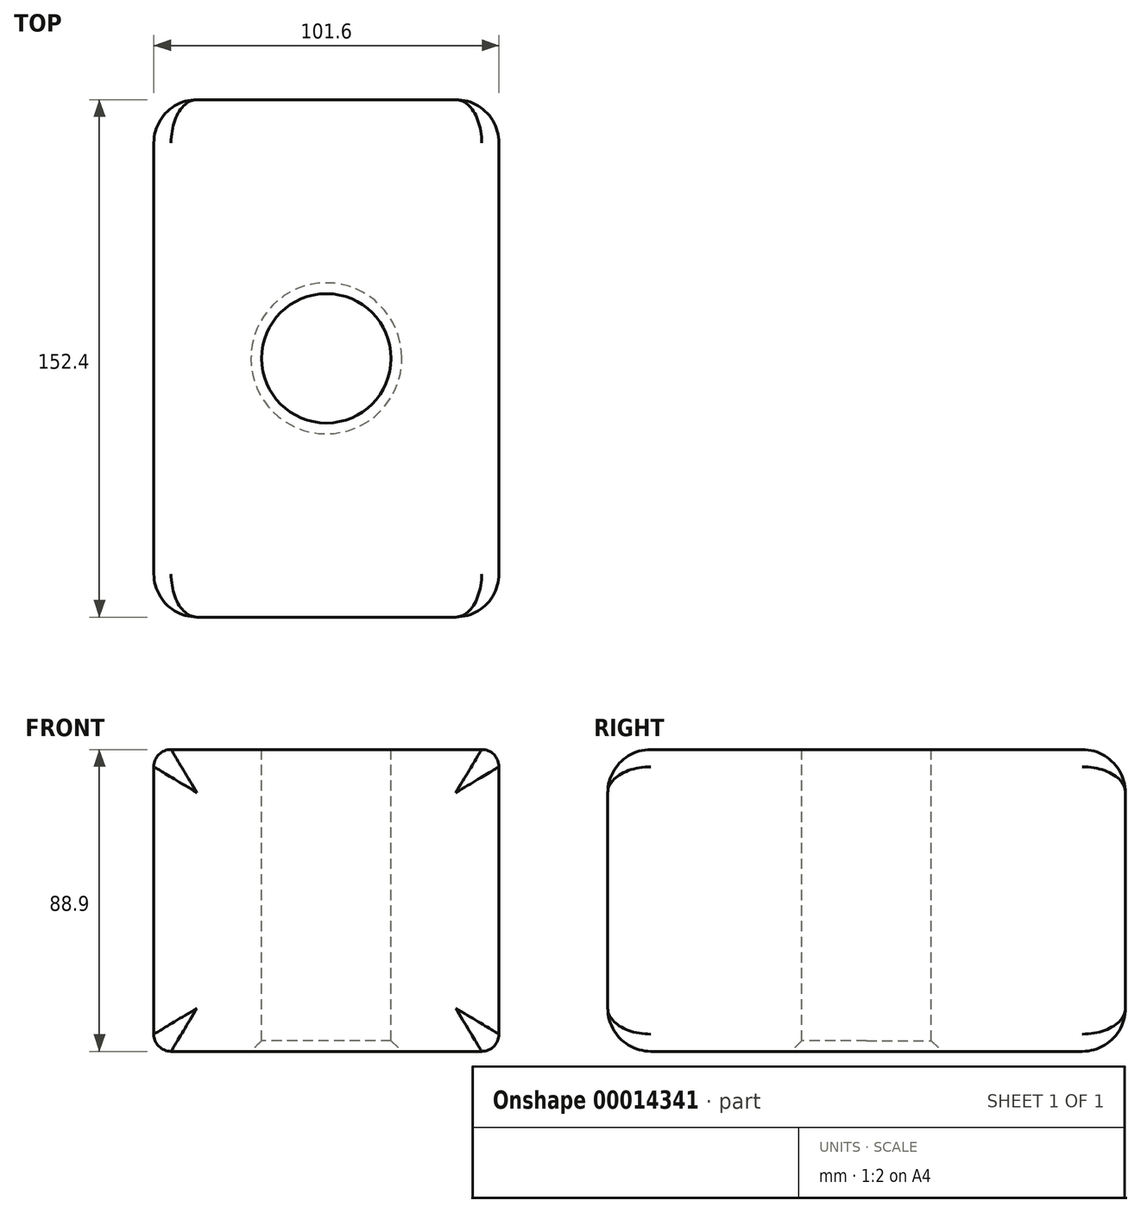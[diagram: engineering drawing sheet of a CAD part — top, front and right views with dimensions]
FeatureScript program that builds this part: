
annotation { "Feature Type Name" : "Feature", "Feature Type Description" : "" }
export const myFeature = defineFeature(function(context is Context, id is Id, definition is map)
    precondition{}
    {
        {
            var Q0;
            Q0=qCreatedBy(makeId("Front.planeOp"),FACE);
            var sketch = newSketch(context, id + "F0", { "sketchPlane" : qUnion([Q0])});
            skLineSegment(sketch, "E0.bottom", {"start": v(0, 0) * mm, "end": v(101.6, 0) * mm});
            skLineSegment(sketch, "E0.top", {"start": v(0, 88.9) * mm, "end": v(101.6, 88.9) * mm});
            skLineSegment(sketch, "E0.left", {"start": v(0, 0) * mm, "end": v(0, 88.9) * mm});
            skLineSegment(sketch, "E0.right", {"start": v(101.6, 0) * mm, "end": v(101.6, 88.9) * mm});
            skSolve(sketch);
        }
        {
            var Q0;
            Q0=makeQuery(id+"F0.imprint","IMPRINT",FACE,{"disambiguationData":[TD([[makeQuery(id+"F0.imprint","IMPRINT",EDGE,{"derivedFrom":sQuery(id+"F0.wireOp",EDGE,"E0.bottom")}),1.0]])]});
            extrude(context, id + "F1", {"entities" : qUnion([Q0]), "oppositeDirection" : true, "depth" : 152.4 * mm});
        }
        {
            var Q0;
            Q0=makeQuery(id+"F1.opExtrude","SWEPT_EDGE",EDGE,{"disambiguationData":[OSD([sQuery(id+"F0.wireOp",EDGE,"E0.top"),sQuery(id+"F0.wireOp",EDGE,"E0.right")])]});
            var Q1;
            Q1=makeQuery(id+"F1.opExtrude","SWEPT_EDGE",EDGE,{"disambiguationData":[OSD([sQuery(id+"F0.wireOp",EDGE,"E0.top"),sQuery(id+"F0.wireOp",EDGE,"E0.left")])]});
            var Q2;
            Q2=makeQuery(id+"F1.opExtrude","SWEPT_EDGE",EDGE,{"disambiguationData":[OSD([sQuery(id+"F0.wireOp",EDGE,"E0.bottom"),sQuery(id+"F0.wireOp",EDGE,"E0.right")])]});
            var Q3;
            Q3=makeQuery(id+"F1.opExtrude","SWEPT_EDGE",EDGE,{"disambiguationData":[OSD([sQuery(id+"F0.wireOp",EDGE,"E0.bottom"),sQuery(id+"F0.wireOp",EDGE,"E0.left")])]});
            fillet(context, id + "F2", {"entities" : qUnion([Q0, Q1, Q2, Q3]), "radius" : 5.08 * mm, "tangentPropagation" : true, "allowEdgeOverflow" : false});
        }
        {
            var Q0;
            Q0=makeQuery(id+"F1.opExtrude","CAP_EDGE",EDGE,{"disambiguationData":[OSD([sQuery(id+"F0.wireOp",EDGE,"E0.left")])],"isStart":true});
            var Q1;
            Q1=makeQuery(id+"F1.opExtrude","CAP_EDGE",EDGE,{"disambiguationData":[OSD([sQuery(id+"F0.wireOp",EDGE,"E0.left")])],"isStart":false});
            fillet(context, id + "F3", {"entities" : qUnion([Q0, Q1]), "radius" : 12.7 * mm, "tangentPropagation" : true, "allowEdgeOverflow" : false});
        }
        {
            var Q0;
            Q0=makeQuery(id+"F1.opExtrude","SWEPT_FACE",FACE,{"disambiguationData":[OSD([sQuery(id+"F0.wireOp",EDGE,"E0.top")])]});
            var sketch = newSketch(context, id + "F4", { "sketchPlane" : qUnion([Q0])});
            skCircle(sketch, "E1", {"center": v(50.8, 76.2) * mm, "radius": 19.05 * mm});
            skLineSegment(sketch, "E2", {"start": v(96.52, 76.2) * mm, "end": v(50.8, 76.2) * mm, "construction": true});
            skLineSegment(sketch, "E3", {"start": v(50.8, 76.2) * mm, "end": v(50.8, 139.7) * mm, "construction": true});
            skSolve(sketch);
        }
        {
            var Q0;
            Q0 = qSketchRegion(id + "F4", true);
            extrude(context, id + "F5", {"entities" : qUnion([Q0]), "operationType" : NewBodyOperationType.REMOVE, "endBound" : BoundingType.THROUGH_ALL, "oppositeDirection" : true, "depth" : 25.4 * mm});
        }
        {
            var Q0;
            Q0=makeQuery(id+"F5.boolean.opBoolean","COPY",EDGE,{"derivedFrom":makeQuery(id+"F5.opExtrude","CAP_EDGE",EDGE,{"disambiguationData":[OSD([sQuery(id+"F4.wireOp",EDGE,"E1")])],"isStart":true})});
            var Q1;
            Q1=makeQuery(id+"F5.boolean.opBoolean","INTERSECT",EDGE,{"derivedFrom":[makeQuery(id+"F1.opExtrude","SWEPT_FACE",FACE,{"disambiguationData":[OSD([sQuery(id+"F0.wireOp",EDGE,"E0.bottom")])]}),makeQuery(id+"F5.opExtrude","SWEPT_FACE",FACE,{"disambiguationData":[OSD([sQuery(id+"F4.wireOp",EDGE,"E1")])]})]});
            chamfer(context, id + "F6", {"entities" : qUnion([Q0, Q1]), "width" : 3.17 * mm, "tangentPropagation" : true});
        }
    });
